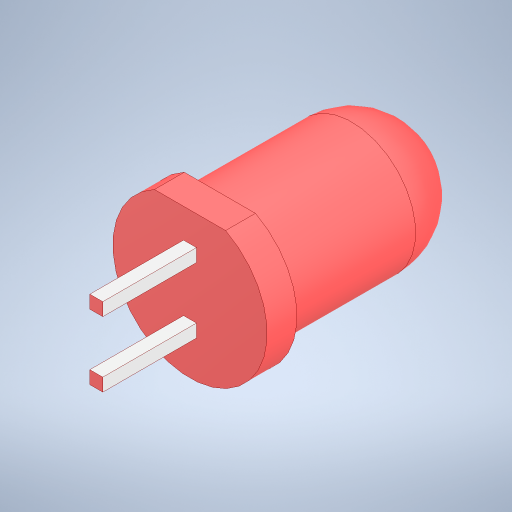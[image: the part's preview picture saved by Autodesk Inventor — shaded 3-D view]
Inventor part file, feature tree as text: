
AUTODESK INVENTOR PART (.ipt)
format: ipt  version: 2023 (Build 270158000, 158)  size: 276,480 bytes
history: mixed  units: in
note: dims shown in document units (in); Inventor stores cm internally (conversion verified against a paired STEP export)
features: other x3, extrude x1, sketch x1, imported_body x1
ambient origin geometry x8: Origin, YZ Plane, XZ Plane, XY Plane, X Axis, Y Axis, Z Axis, Center Point
bodies: Solid1 (imported_parasolid)
feature tree (6):
  other  "red-led-5mm.ipt"
  extrude  "Extrusion1"  Depth=0.3937in TaperAngle=0.0deg
  other  "Solid1::red-led-5mm.ipt"
  other  "TaggingFeature1"
  sketch  "Sketch1"  dims[d0=0.3937in d1=0.3937in d2=0.0in]
  imported_body  NMx_Import_Brep_tag  [imported B-rep: ~16 faces, bbox_mm=[4.94, 4.15, 9.8425]]
